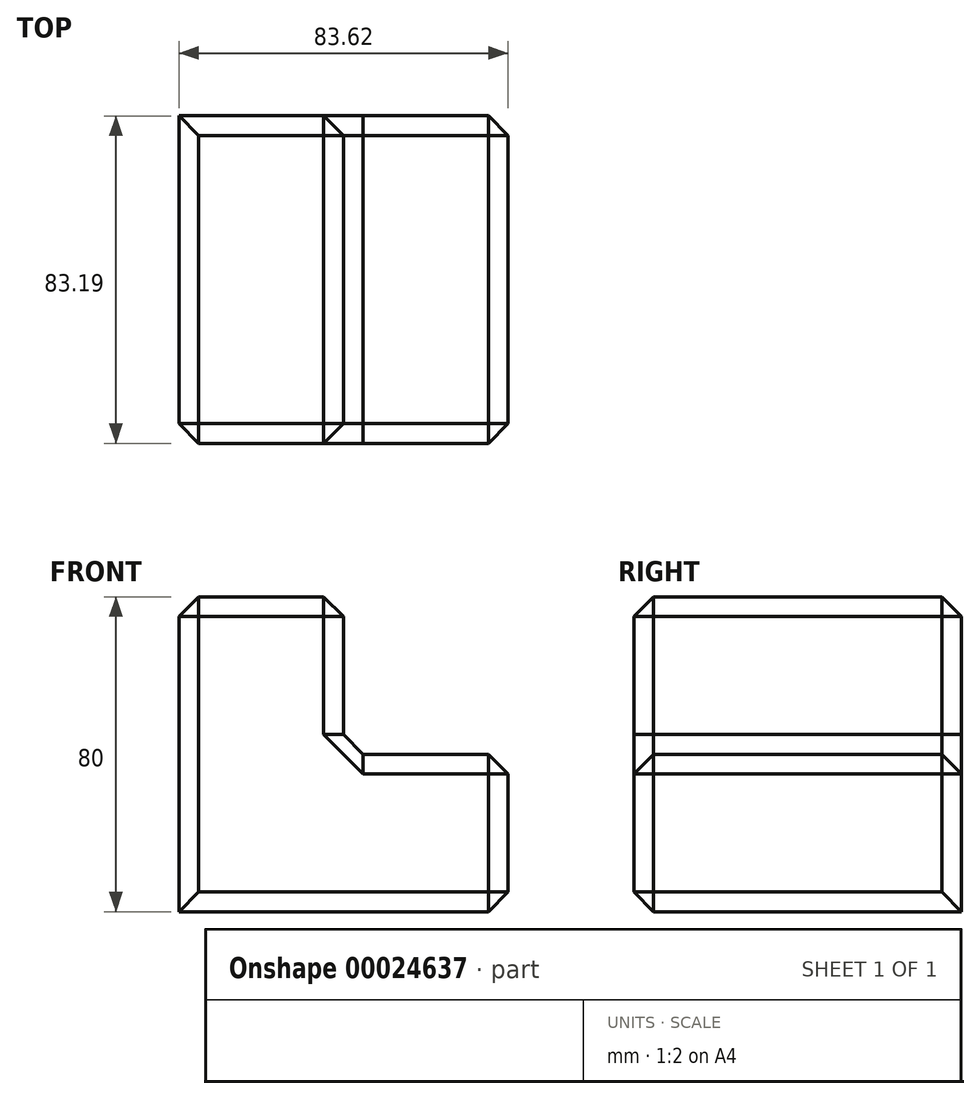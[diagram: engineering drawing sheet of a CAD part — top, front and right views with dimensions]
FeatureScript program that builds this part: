
annotation { "Feature Type Name" : "Feature", "Feature Type Description" : "" }
export const myFeature = defineFeature(function(context is Context, id is Id, definition is map)
    precondition{}
    {
        {
            var Q0;
            Q0=qCreatedBy(makeId("Top.planeOp"),FACE);
            var sketch = newSketch(context, id + "F0", { "sketchPlane" : qUnion([Q0])});
            skLineSegment(sketch, "E0.bottom", {"start": v(-59.13, -45.93) * mm, "end": v(24.5, -45.93) * mm});
            skLineSegment(sketch, "E0.top", {"start": v(-59.13, 37.26) * mm, "end": v(24.5, 37.26) * mm});
            skLineSegment(sketch, "E0.left", {"start": v(-59.13, -45.93) * mm, "end": v(-59.13, 37.26) * mm});
            skLineSegment(sketch, "E0.right", {"start": v(24.5, -45.93) * mm, "end": v(24.5, 37.26) * mm});
            skSolve(sketch);
        }
        {
            var Q0;
            Q0=makeQuery(id+"F0.imprint","IMPRINT",FACE,{"disambiguationData":[TD([[makeQuery(id+"F0.imprint","IMPRINT",EDGE,{"derivedFrom":sQuery(id+"F0.wireOp",EDGE,"E0.bottom")}),1.0]])]});
            extrude(context, id + "F1", {"entities" : qUnion([Q0]), "depth" : 40 * mm});
        }
        {
            var Q0;
            Q0=makeQuery(id+"F1.opExtrude","CAP_FACE",FACE,{"disambiguationData":[OSD([sQuery(id+"F0.wireOp",EDGE,"E0.bottom"),sQuery(id+"F0.wireOp",EDGE,"E0.top"),sQuery(id+"F0.wireOp",EDGE,"E0.left"),sQuery(id+"F0.wireOp",EDGE,"E0.right")])],"isStart":false});
            var sketch = newSketch(context, id + "F2", { "sketchPlane" : qUnion([Q0])});
            skLineSegment(sketch, "E1", {"start": v(-17.32, 37.26) * mm, "end": v(-17.32, -45.93) * mm});
            skSolve(sketch);
        }
        {
            var Q0;
            {var subQ1=sQuery(id+"F2.wireOp",EDGE,"E1");Q0=makeQuery(id+"F2.imprint","IMPRINT",FACE,{"disambiguationData":[TD([[makeQuery(id+"F2.imprint","IMPRINT",EDGE,{"derivedFrom":subQ1}),-1.0]])]});}
            extrude(context, id + "F3", {"entities" : qUnion([Q0]), "operationType" : NewBodyOperationType.ADD, "depth" : 40 * mm});
        }
        {
            var Q0;
            {var subQ0=sQuery(id+"F0.wireOp",EDGE,"E0.bottom");Q0=makeQuery(id+"F3.boolean.opBoolean","MERGE",FACE,{"derivedFrom":[makeQuery(id+"F1.opExtrude","SWEPT_FACE",FACE,{"disambiguationData":[OSD([subQ0])]}),makeQuery(id+"F3.opExtrude","SWEPT_FACE",FACE,{"disambiguationData":[OSD([subQ0])]})]});}
            var Q1;
            Q1=makeQuery(id+"F3.opExtrude","CAP_FACE",FACE,{"disambiguationData":[OSD([sQuery(id+"F0.wireOp",EDGE,"E0.bottom"),sQuery(id+"F0.wireOp",EDGE,"E0.top"),sQuery(id+"F0.wireOp",EDGE,"E0.left"),sQuery(id+"F2.wireOp",EDGE,"E1")])],"isStart":false});
            var Q2;
            Q2=makeQuery(id+"F3.opExtrude","SWEPT_FACE",FACE,{"disambiguationData":[OSD([sQuery(id+"F2.wireOp",EDGE,"E1")])]});
            var Q3;
            Q3=makeQuery(id+"F1.opExtrude","CAP_FACE",FACE,{"disambiguationData":[OSD([sQuery(id+"F0.wireOp",EDGE,"E0.bottom"),sQuery(id+"F0.wireOp",EDGE,"E0.top"),sQuery(id+"F0.wireOp",EDGE,"E0.left"),sQuery(id+"F0.wireOp",EDGE,"E0.right")])],"isStart":false});
            var Q4;
            Q4=makeQuery(id+"F1.opExtrude","SWEPT_FACE",FACE,{"disambiguationData":[OSD([sQuery(id+"F0.wireOp",EDGE,"E0.right")])]});
            chamfer(context, id + "F4", {"entities" : qUnion([Q0, Q1, Q2, Q3, Q4]), "width" : 5 * mm, "tangentPropagation" : true});
        }
    });
